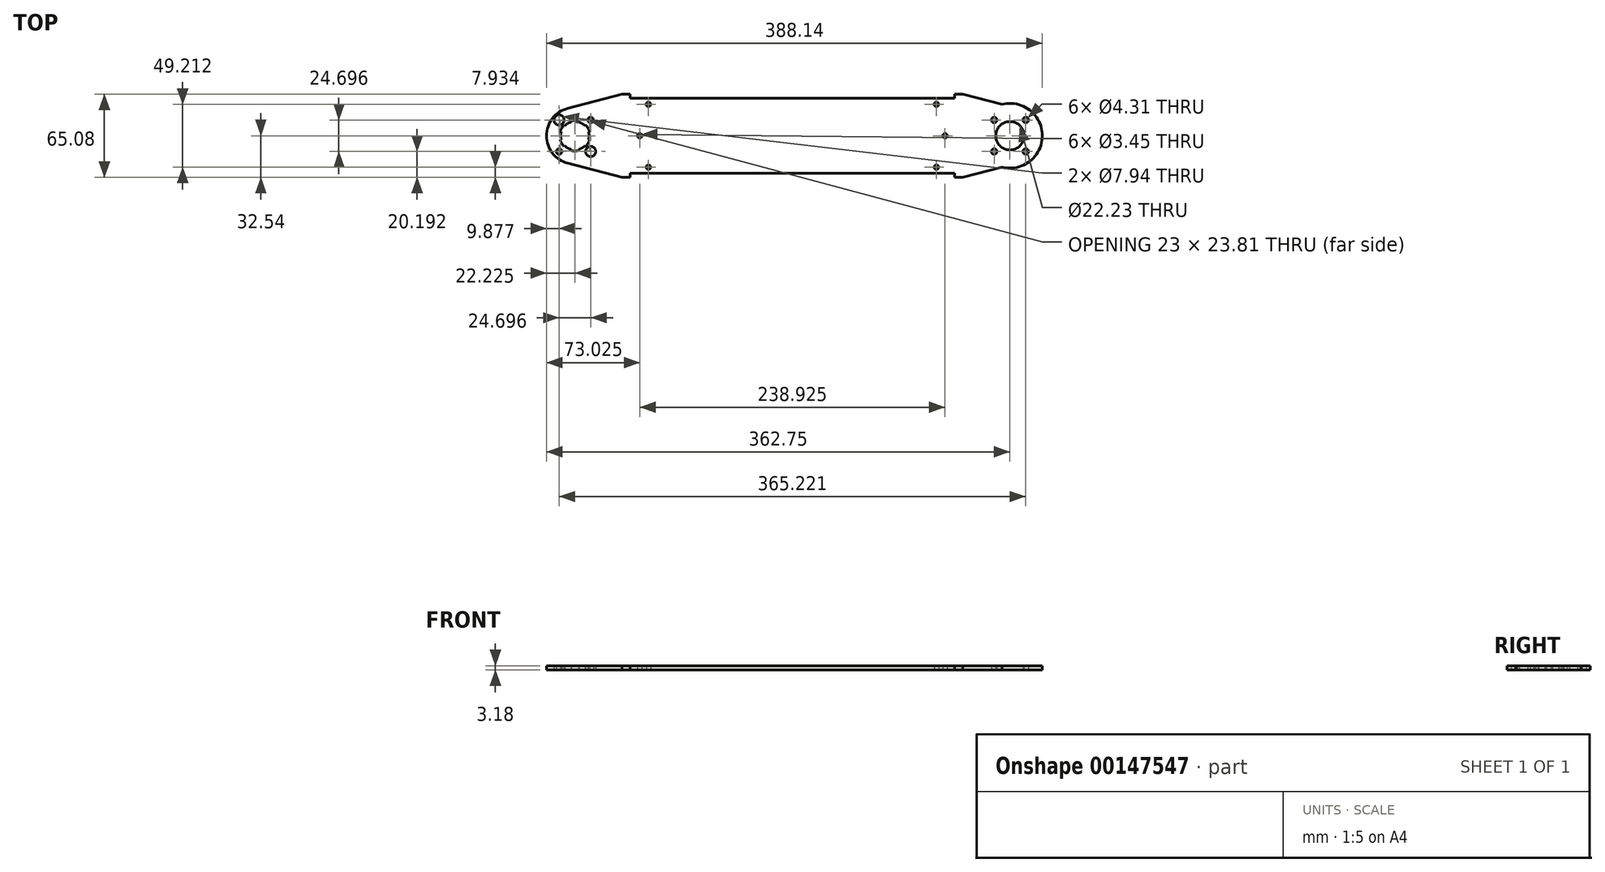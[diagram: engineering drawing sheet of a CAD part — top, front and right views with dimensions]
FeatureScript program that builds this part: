
annotation { "Feature Type Name" : "Feature", "Feature Type Description" : "" }
export const myFeature = defineFeature(function(context is Context, id is Id, definition is map)
    precondition{}
    {
        {
            var Q0;
            Q0=qCreatedBy(makeId("Top.planeOp"),FACE);
            var sketch = newSketch(context, id + "F0", { "sketchPlane" : qUnion([Q0])});
            skPoint(sketch, "E0.rect.middle", {"position": v(0, 0) * mm});
            skCircle(sketch, "E1", {"center": v(0, 0) * mm, "radius": 11.11 * mm});
            skLineSegment(sketch, "E2.bottom", {"start": v(12.35, 12.35) * mm, "end": v(-12.35, 12.35) * mm, "construction": true});
            skLineSegment(sketch, "E2.left", {"start": v(12.35, 12.35) * mm, "end": v(12.35, -12.35) * mm, "construction": true});
            skLineSegment(sketch, "E2.right", {"start": v(-12.35, 12.35) * mm, "end": v(-12.35, -12.35) * mm, "construction": true});
            skCircle(sketch, "E3", {"center": v(-12.35, 12.35) * mm, "radius": 2.15 * mm});
            skCircle(sketch, "E4", {"center": v(12.35, 12.35) * mm, "radius": 2.15 * mm});
            skCircle(sketch, "E5", {"center": v(12.35, -12.35) * mm, "radius": 2.15 * mm});
            skCircle(sketch, "E6", {"center": v(-12.35, -12.35) * mm, "radius": 2.15 * mm});
            skArc(sketch, "E7", {"start": v(-346.1, 21.51) * mm, "mid": v(-362.75, 0) * mm, "end": v(-346.1, -21.51) * mm});
            skLineSegment(sketch, "E8.bottom", {"start": v(-352.87, 12.35) * mm, "end": v(-328.18, 12.35) * mm, "construction": true});
            skLineSegment(sketch, "E8.top", {"start": v(-352.87, -12.35) * mm, "end": v(-328.18, -12.35) * mm, "construction": true});
            skLineSegment(sketch, "E8.left", {"start": v(-352.87, 12.35) * mm, "end": v(-352.87, -12.35) * mm, "construction": true});
            skLineSegment(sketch, "E8.right", {"start": v(-328.18, 12.35) * mm, "end": v(-328.18, -12.35) * mm, "construction": true});
            skCircle(sketch, "E9", {"center": v(-328.18, 12.35) * mm, "radius": 2.15 * mm});
            skCircle(sketch, "E10", {"center": v(-340.53, 0) * mm, "radius": 11.11 * mm});
            skCircle(sketch, "E11", {"center": v(-352.87, 12.35) * mm, "radius": 3.97 * mm});
            skCircle(sketch, "E12", {"center": v(-352.87, -12.35) * mm, "radius": 2.15 * mm});
            skCircle(sketch, "E13", {"center": v(-328.18, -12.35) * mm, "radius": 3.97 * mm});
            skLineSegment(sketch, "E14", {"start": v(0, 0) * mm, "end": v(-340.53, 0) * mm, "construction": true});
            skLineSegment(sketch, "E15", {"start": v(-346.1, -21.51) * mm, "end": v(-303.61, -32.54) * mm});
            skLineSegment(sketch, "E16", {"start": v(-346.1, 21.51) * mm, "end": v(-303.61, 32.54) * mm});
            skLineSegment(sketch, "E17", {"start": v(-297.26, -29.37) * mm, "end": v(-43.26, -29.37) * mm});
            skLineSegment(sketch, "E18", {"start": v(-297.26, 29.37) * mm, "end": v(-43.26, 29.37) * mm});
            skLineSegment(sketch, "E19", {"start": v(-297.26, 32.54) * mm, "end": v(-297.26, 29.37) * mm});
            skLineSegment(sketch, "E20", {"start": v(-297.26, 32.54) * mm, "end": v(-303.61, 32.54) * mm});
            skLineSegment(sketch, "E21", {"start": v(-297.26, -29.37) * mm, "end": v(-297.26, -32.54) * mm});
            skLineSegment(sketch, "E22", {"start": v(-297.26, -32.54) * mm, "end": v(-303.61, -32.54) * mm});
            skLineSegment(sketch, "E23", {"start": v(-43.26, -29.37) * mm, "end": v(-43.26, -32.54) * mm});
            skLineSegment(sketch, "E24", {"start": v(-43.26, -32.54) * mm, "end": v(-36.91, -32.54) * mm});
            skLineSegment(sketch, "E25", {"start": v(-43.26, 29.37) * mm, "end": v(-43.26, 32.54) * mm});
            skLineSegment(sketch, "E26", {"start": v(-43.26, 32.54) * mm, "end": v(-36.91, 32.54) * mm});
            skLineSegment(sketch, "E27", {"start": v(-36.91, -32.54) * mm, "end": v(-6.3, -24.6) * mm});
            skLineSegment(sketch, "E28", {"start": v(-6.3, 24.6) * mm, "end": v(-36.91, 32.54) * mm});
            skLineSegment(sketch, "E29", {"start": v(-297.26, 29.37) * mm, "end": v(-297.26, 24.6) * mm, "construction": true});
            skLineSegment(sketch, "E30", {"start": v(-297.26, 24.6) * mm, "end": v(-282.98, 24.6) * mm, "construction": true});
            skLineSegment(sketch, "E31", {"start": v(-297.26, -29.37) * mm, "end": v(-297.26, -24.6) * mm, "construction": true});
            skLineSegment(sketch, "E32", {"start": v(-297.26, -24.6) * mm, "end": v(-282.98, -24.6) * mm, "construction": true});
            skLineSegment(sketch, "E33", {"start": v(-43.26, -29.37) * mm, "end": v(-43.26, -24.6) * mm, "construction": true});
            skLineSegment(sketch, "E34", {"start": v(-43.26, -24.6) * mm, "end": v(-57.55, -24.6) * mm, "construction": true});
            skLineSegment(sketch, "E35", {"start": v(-43.26, 29.37) * mm, "end": v(-43.26, 24.6) * mm, "construction": true});
            skLineSegment(sketch, "E36", {"start": v(-43.26, 24.6) * mm, "end": v(-57.55, 24.6) * mm, "construction": true});
            skCircle(sketch, "E37", {"center": v(-282.98, 24.6) * mm, "radius": 1.73 * mm});
            skCircle(sketch, "E38", {"center": v(-57.55, 24.6) * mm, "radius": 1.73 * mm});
            skCircle(sketch, "E39", {"center": v(-57.55, -24.6) * mm, "radius": 1.73 * mm});
            skCircle(sketch, "E40", {"center": v(-282.98, -24.6) * mm, "radius": 1.73 * mm});
            skLineSegment(sketch, "E41", {"start": v(-12.35, -12.35) * mm, "end": v(12.35, -12.35) * mm, "construction": true});
            skLineSegment(sketch, "E42", {"start": v(-170.26, -29.37) * mm, "end": v(-170.26, 0) * mm, "construction": true});
            skLineSegment(sketch, "E43", {"start": v(-170.26, 0) * mm, "end": v(-170.26, 29.37) * mm, "construction": true});
            skArc(sketch, "E44", {"start": v(-6.3, -24.6) * mm, "mid": v(25.4, 0) * mm, "end": v(-6.3, 24.6) * mm});
            skLineSegment(sketch, "E45", {"start": v(-6.3, 24.6) * mm, "end": v(5.58, 21.51) * mm, "construction": true});
            skLineSegment(sketch, "E46", {"start": v(-6.3, -24.6) * mm, "end": v(5.58, -21.51) * mm, "construction": true});
            skArc(sketch, "E47", {"start": v(5.58, -21.51) * mm, "mid": v(22.23, 0) * mm, "end": v(5.58, 21.51) * mm, "construction": true});
            skLineSegment(sketch, "E48", {"start": v(-328.18, 12.35) * mm, "end": v(-289.73, 12.35) * mm, "construction": true});
            skLineSegment(sketch, "E49", {"start": v(-289.73, 12.35) * mm, "end": v(-289.73, 0) * mm, "construction": true});
            skLineSegment(sketch, "E50", {"start": v(-12.35, 12.35) * mm, "end": v(-50.8, 12.35) * mm, "construction": true});
            skLineSegment(sketch, "E51", {"start": v(-50.8, 12.35) * mm, "end": v(-50.8, 0) * mm, "construction": true});
            skCircle(sketch, "E52", {"center": v(-289.73, 0) * mm, "radius": 1.73 * mm});
            skCircle(sketch, "E53", {"center": v(-50.8, 0) * mm, "radius": 1.73 * mm});
            skSolve(sketch);
        }
        {
            var Q0;
            Q0=qSketchRegion(id+"F0",true);
            extrude(context, id + "F1", {"entities" : qUnion([Q0]), "depth" : 3.17 * mm});
        }
        {
            var Q0;
            Q0=makeQuery(id+"F1.opExtrude","CAP_FACE",FACE,{"disambiguationData":[OSD([sQuery(id+"F0.wireOp",EDGE,"d63eafa0-1946-4b0e-8293-95e246b273c5.rect.bottom"),sQuery(id+"F0.wireOp",EDGE,"d63eafa0-1946-4b0e-8293-95e246b273c5.rect.top"),sQuery(id+"F0.wireOp",EDGE,"5983dcdd-59a7-4b72-80fd-e4567be1ae8a"),sQuery(id+"F0.wireOp",EDGE,"5a538b3e-fc2b-4d64-affd-5d60433388e5"),sQuery(id+"F0.wireOp",EDGE,"72e86de7-b207-474f-aadf-64543fae3f9b"),sQuery(id+"F0.wireOp",EDGE,"1c038800-5bd5-4753-8b38-6da13ef78ef9"),sQuery(id+"F0.wireOp",EDGE,"EbMUZoU6-Ffds-1dNq-SxhE-hPi8oSjhvaod"),sQuery(id+"F0.wireOp",EDGE,"RfgQjzcw-1Izs-lnTa-bWkk-oBHRDQjbZqQC"),sQuery(id+"F0.wireOp",EDGE,"1cCQAcjj-TyQA-3DMx-kDix-v5yZVaaGeXVM"),sQuery(id+"F0.wireOp",EDGE,"7KPu8lni-3ZWA-t6oJ-FRoh-C5MB3aVr7E9B"),sQuery(id+"F0.wireOp",EDGE,"bSzr06ES-7M0i-Fw5H-UJmt-4e4EQGRPIe4n"),sQuery(id+"F0.wireOp",EDGE,"WGsr6OjU-OX8l-mawA-7cCc-MfOuMOY06Cp5"),sQuery(id+"F0.wireOp",EDGE,"9mrz1cDN-18gM-20ra-6VCO-jp25g10tvNn2"),sQuery(id+"F0.wireOp",EDGE,"G0uOisy3-Mq6h-PcKh-Zkf4-CVoCvP3Hii1l"),sQuery(id+"F0.wireOp",EDGE,"1ae556be-0ab9-4322-b48e-98cf5a741ae0"),sQuery(id+"F0.wireOp",EDGE,"676cd913-43f8-42b3-8cdc-a90136d19ef5"),sQuery(id+"F0.wireOp",EDGE,"xnt2EyF8-ZVyQ-RbWD-GIsP-ThkcyX8ZioIH.bottom"),sQuery(id+"F0.wireOp",EDGE,"xnt2EyF8-ZVyQ-RbWD-GIsP-ThkcyX8ZioIH.top"),sQuery(id+"F0.wireOp",EDGE,"xnt2EyF8-ZVyQ-RbWD-GIsP-ThkcyX8ZioIH.left"),sQuery(id+"F0.wireOp",EDGE,"E1"),sQuery(id+"F0.wireOp",EDGE,"Jo9pZc7T-t0kF-vjz1-dNbX-L65bwNqtrrdz"),sQuery(id+"F0.wireOp",EDGE,"lEYoY9t7-PMOS-SVp6-xfnB-Xp9WdWMCDdum"),sQuery(id+"F0.wireOp",EDGE,"s7aM02SC-9XQ7-dueL-DqMg-ZFuJqOofj9mt"),sQuery(id+"F0.wireOp",EDGE,"deKa9ngt-XMq2-GGkr-SZIa-KlyN0U5bcCDe"),sQuery(id+"F0.wireOp",EDGE,"E3"),sQuery(id+"F0.wireOp",EDGE,"E4"),sQuery(id+"F0.wireOp",EDGE,"E5"),sQuery(id+"F0.wireOp",EDGE,"E6"),sQuery(id+"F0.wireOp",EDGE,"E7"),sQuery(id+"F0.wireOp",EDGE,"E9"),sQuery(id+"F0.wireOp",EDGE,"E10"),sQuery(id+"F0.wireOp",EDGE,"E11"),sQuery(id+"F0.wireOp",EDGE,"E12"),sQuery(id+"F0.wireOp",EDGE,"E13")])],"isStart":true});
            var sketch = newSketch(context, id + "F2", { "sketchPlane" : qUnion([Q0])});
            skLineSegment(sketch, "E54", {"start": v(-340.53, 0) * mm, "end": v(-350.15, -5.56) * mm, "construction": true});
            skArc(sketch, "E55", {"start": v(-351.26, -2.88) * mm, "mid": v(-350.15, -5.56) * mm, "end": v(-348.38, -7.86) * mm});
            skLineSegment(sketch, "E56", {"start": v(-340.53, 0) * mm, "end": v(-348.38, -7.86) * mm, "construction": true});
            skLineSegment(sketch, "E57", {"start": v(-340.53, 0) * mm, "end": v(-351.26, -2.88) * mm, "construction": true});
            skLineSegment(sketch, "E58", {"start": v(-348.38, -7.86) * mm, "end": v(-348.94, -8.42) * mm});
            skLineSegment(sketch, "E59", {"start": v(-351.26, -2.88) * mm, "end": v(-352.03, -3.08) * mm});
            skArc(sketch, "E60", {"start": v(-352.03, -3.08) * mm, "mid": v(-350.84, -5.95) * mm, "end": v(-348.94, -8.42) * mm});
            skLineSegment(sketch, "E61", {"start": v(-340.53, 0) * mm, "end": v(-351.64, 0) * mm, "construction": true});
            skSolve(sketch);
        }
        {
            var Q0;
            Q0=qSketchRegion(id+"F2",true);
            var Q1;
            Q1=makeQuery(id+"F1.opExtrude","CAP_FACE",FACE,{"disambiguationData":[OSD([sQuery(id+"F0.wireOp",EDGE,"d63eafa0-1946-4b0e-8293-95e246b273c5.rect.bottom"),sQuery(id+"F0.wireOp",EDGE,"d63eafa0-1946-4b0e-8293-95e246b273c5.rect.top"),sQuery(id+"F0.wireOp",EDGE,"5983dcdd-59a7-4b72-80fd-e4567be1ae8a"),sQuery(id+"F0.wireOp",EDGE,"5a538b3e-fc2b-4d64-affd-5d60433388e5"),sQuery(id+"F0.wireOp",EDGE,"72e86de7-b207-474f-aadf-64543fae3f9b"),sQuery(id+"F0.wireOp",EDGE,"1c038800-5bd5-4753-8b38-6da13ef78ef9"),sQuery(id+"F0.wireOp",EDGE,"EbMUZoU6-Ffds-1dNq-SxhE-hPi8oSjhvaod"),sQuery(id+"F0.wireOp",EDGE,"RfgQjzcw-1Izs-lnTa-bWkk-oBHRDQjbZqQC"),sQuery(id+"F0.wireOp",EDGE,"1cCQAcjj-TyQA-3DMx-kDix-v5yZVaaGeXVM"),sQuery(id+"F0.wireOp",EDGE,"7KPu8lni-3ZWA-t6oJ-FRoh-C5MB3aVr7E9B"),sQuery(id+"F0.wireOp",EDGE,"bSzr06ES-7M0i-Fw5H-UJmt-4e4EQGRPIe4n"),sQuery(id+"F0.wireOp",EDGE,"WGsr6OjU-OX8l-mawA-7cCc-MfOuMOY06Cp5"),sQuery(id+"F0.wireOp",EDGE,"9mrz1cDN-18gM-20ra-6VCO-jp25g10tvNn2"),sQuery(id+"F0.wireOp",EDGE,"G0uOisy3-Mq6h-PcKh-Zkf4-CVoCvP3Hii1l"),sQuery(id+"F0.wireOp",EDGE,"1ae556be-0ab9-4322-b48e-98cf5a741ae0"),sQuery(id+"F0.wireOp",EDGE,"676cd913-43f8-42b3-8cdc-a90136d19ef5"),sQuery(id+"F0.wireOp",EDGE,"xnt2EyF8-ZVyQ-RbWD-GIsP-ThkcyX8ZioIH.bottom"),sQuery(id+"F0.wireOp",EDGE,"xnt2EyF8-ZVyQ-RbWD-GIsP-ThkcyX8ZioIH.top"),sQuery(id+"F0.wireOp",EDGE,"xnt2EyF8-ZVyQ-RbWD-GIsP-ThkcyX8ZioIH.left"),sQuery(id+"F0.wireOp",EDGE,"E1"),sQuery(id+"F0.wireOp",EDGE,"Jo9pZc7T-t0kF-vjz1-dNbX-L65bwNqtrrdz"),sQuery(id+"F0.wireOp",EDGE,"lEYoY9t7-PMOS-SVp6-xfnB-Xp9WdWMCDdum"),sQuery(id+"F0.wireOp",EDGE,"s7aM02SC-9XQ7-dueL-DqMg-ZFuJqOofj9mt"),sQuery(id+"F0.wireOp",EDGE,"deKa9ngt-XMq2-GGkr-SZIa-KlyN0U5bcCDe"),sQuery(id+"F0.wireOp",EDGE,"E3"),sQuery(id+"F0.wireOp",EDGE,"E4"),sQuery(id+"F0.wireOp",EDGE,"E5"),sQuery(id+"F0.wireOp",EDGE,"E6"),sQuery(id+"F0.wireOp",EDGE,"E7"),sQuery(id+"F0.wireOp",EDGE,"E9"),sQuery(id+"F0.wireOp",EDGE,"E10"),sQuery(id+"F0.wireOp",EDGE,"E11"),sQuery(id+"F0.wireOp",EDGE,"E12"),sQuery(id+"F0.wireOp",EDGE,"E13")])],"isStart":false});
            extrude(context, id + "F3", {"entities" : qUnion([Q0]), "operationType" : NewBodyOperationType.REMOVE, "endBound" : BoundingType.UP_TO_SURFACE, "oppositeDirection" : true, "endBoundEntityFace" : qUnion([Q1]), "depth" : 25.4 * mm});
        }
        {
            var Q0;
            Q0=makeQuery(id+"F3.boolean.opBoolean","COPY",FACE,{"derivedFrom":makeQuery(id+"F3.opExtrude","SWEPT_FACE",FACE,{"disambiguationData":[OSD([sQuery(id+"F2.wireOp",EDGE,"E58")])]})});
            var Q1;
            Q1=makeQuery(id+"F3.boolean.opBoolean","COPY",FACE,{"derivedFrom":makeQuery(id+"F3.opExtrude","SWEPT_FACE",FACE,{"disambiguationData":[OSD([sQuery(id+"F2.wireOp",EDGE,"E60")])]})});
            var Q2;
            Q2=makeQuery(id+"F3.boolean.opBoolean","COPY",FACE,{"derivedFrom":makeQuery(id+"F3.opExtrude","SWEPT_FACE",FACE,{"disambiguationData":[OSD([sQuery(id+"F2.wireOp",EDGE,"E59")])]})});
            var Q3;
            Q3=makeQuery(id+"F1.opExtrude","SWEPT_FACE",FACE,{"disambiguationData":[OSD([sQuery(id+"F0.wireOp",EDGE,"E10")])]});
            circularPattern(context, id + "F4", {"patternType" : PatternType.FACE, "faces" : qUnion([Q0, Q1, Q2]), "axis" : qUnion([Q3]), "angle" : 60 * degree, "instanceCount" : 6});
        }
    });
